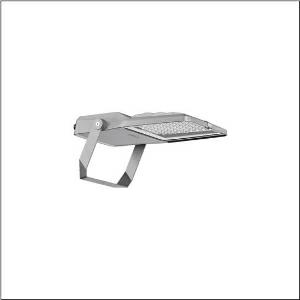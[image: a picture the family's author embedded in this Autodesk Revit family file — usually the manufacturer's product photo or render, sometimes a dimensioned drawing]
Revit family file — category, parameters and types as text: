
# Revit family: floodlight_fl_21_iq_mini___pl33t_5xa7772d2f1a_a564
name_source: partatom
category: Lighting Fixtures
units: mm (PartAtom-declared; Revit-internal decimal feet)

## family parameters
Cut with Voids When Loaded = No
Host = Face
Light Source = No
Part Type = Normal
Room Calculation Point = No
Round Connector Dimension = Use Diameter
Shared = No

## types (1)
- --- (1 x LED, 17620 lm, 143 W, 3000K)
    Apparent Load = 143 VA
    CIE Flux Codes = 26 75 99 100 100
    Color Rendering = 70
    Color Temperature = 3000K
    Default Elevation = 1800 mm
    Description = Floodlight FL 21 iQ mini, floodlight, primary light control with lens, of PMMA, primary optical cover: protective disc, of toughened safety glass, transparent, light distribution: PL33T, light emission: direct distribution, installation type: surface-mounted, lamps: LED, High Power LED, rated values: 17.620lm | 143W | 123,2lm/W (begin service life); end service life: 17.620lm | 151,6W; at 50% lumin. flux: 8.810lm | 60,6W | 145,4lm/W, colour temperature: 3000K, colour rendering: CRI > 70, light colour: 730, light setting 1 begin service life: 100% | 17.620lm | 143W | 123,2lm/W | 3.000K, light setting 1 end service life: 151,6W, further light settings possible, control: Street-Remote, Auto-Match, Temp-Guard, Night-Set, Smart-Wire, Desk-Remote (wireless, voltage-free reading and setting of iQ features in the workshop via application-optimized NFC function/RFID function), optimised constant luminous flux control (CLO 2.0), pre-setting: linear dimming characteristic, with terminal, 6-pole, mains connection: 220..240V, AC, 50/60Hz, luminaire housing, of diecast aluminium, powder-coated, SITECO metallic grey (DB 702S), corrosivity category C5 mid according to DIN EN ISO 12944suitable for swimming poolschlorine-resistant, sealing non-destructively replaceable, mounting bracket, of steel, galvanised, powder-coated, SITECO metallic grey (DB 702S), protection rating (complete): IP66, insulation class (complete): insulation class II (safety insulation), certification: CE, ENEC, VDE, protection symbol: D, impact resistance: IK08, permissible operating ambient temperature: -40..+40°C, permissible operating ambient temperature for outdoor applications: -40..+50°C, standard: DIN EN 12944, LABS conformity tested according to VDMA 24364:2018-05, packaging unit: 1 piece

Light Distribution: PL33T
    Height = 70 mm
    Lamp = 1 x LED
    Lamp Light Flux = 17620 lm
    Lamp Power = 143 W
    Lamp count = 1
    Length = 485 mm
    Luminous efficacy = 123 lm/W
    Manufacturer = Siteco
    ModVariant = No
    Model = 5XA7772D2F1A
    Number of Poles = 1
    OnlyDefault = Yes
    Power Factor = 1
    Product Name = Floodlight FL 21 iQ mini | PL33T
    Product group = floodlight | pylon annexe
    ProductGroupID = 6201
    Protection Class = Protection class II
    Protection Degree = IP 66
    RLX_Detail_Level = 1
    RLX_Emergency_Light_Flux = 0 lm
    RLX_Emergency_Type = 0
    RLX_Emergency_Type_DB = No
    RlxData = <blob elided: 96673 chars, md5=72e490a7>
    Socket = socket
    Standby Power = 0 W
    System Light Flux = 17620 lm
    System Power = 143 W
    Type Comments = factory setting: luminous flux: 100 % | dim-lin: 254 | 730 mA
    Type Image = l_1006845.jpg
    URL = http://relux.com
    VarID = @adj_148503
    Voltage = 0 V
    Weight = 0.00 kg
    Width = 337 mm

## geometry (parser evidence)
native form markers: Blend x4, Sweep x12
no freeform markers — native parametric forms only
